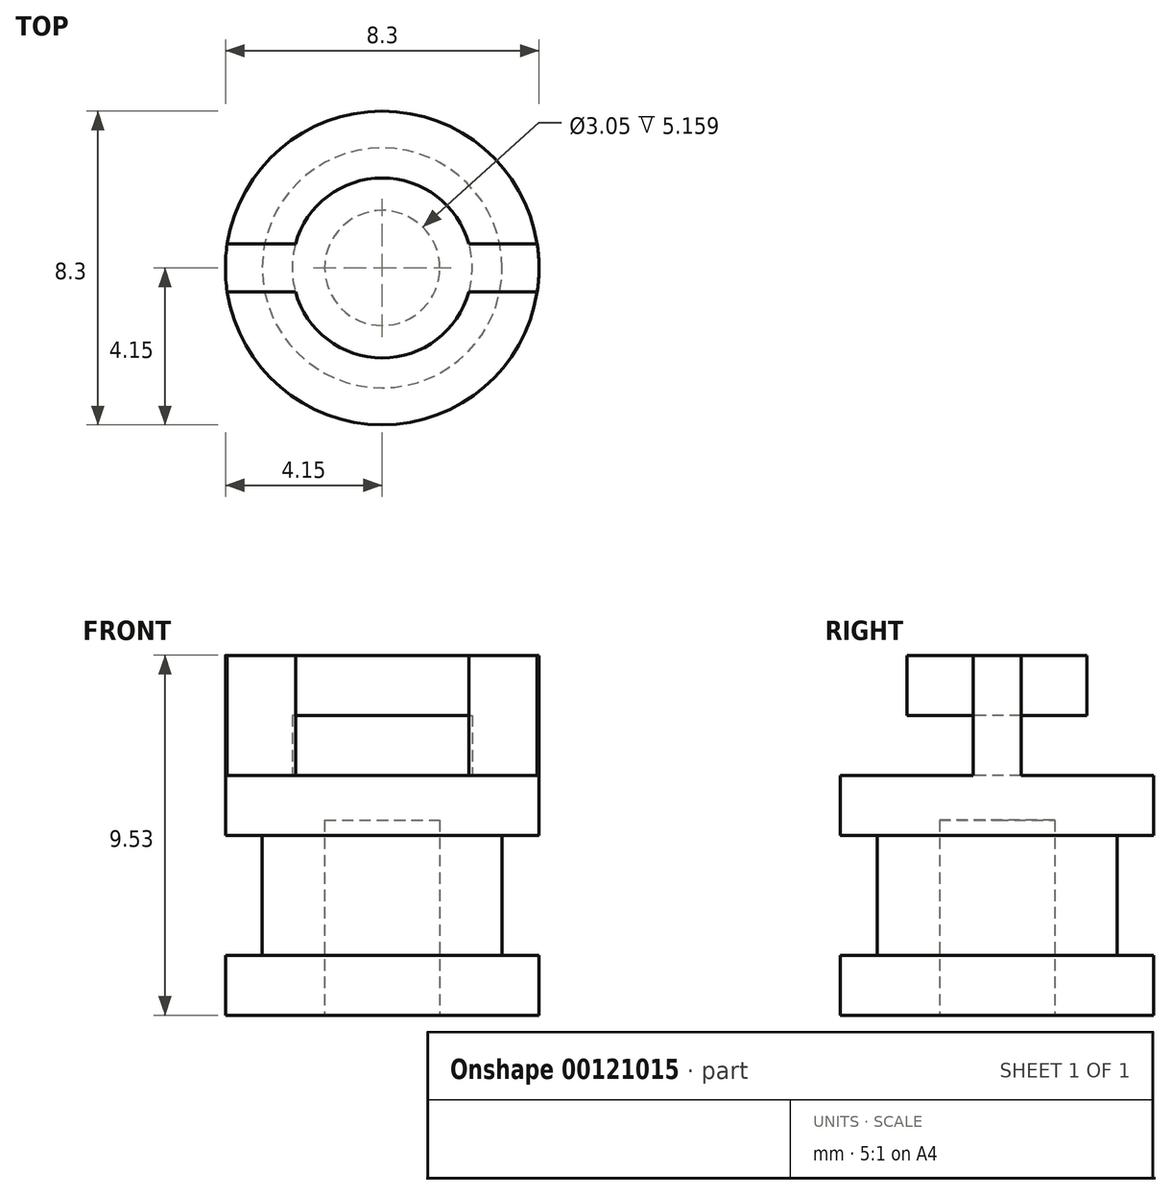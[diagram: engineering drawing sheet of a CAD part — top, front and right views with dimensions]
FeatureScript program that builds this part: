
annotation { "Feature Type Name" : "Feature", "Feature Type Description" : "" }
export const myFeature = defineFeature(function(context is Context, id is Id, definition is map)
    precondition{}
    {
        {
            var Q0;
            Q0=qCreatedBy(makeId("Top.planeOp"),FACE);
            var sketch = newSketch(context, id + "F0", { "sketchPlane" : qUnion([Q0])});
            skCircle(sketch, "E0", {"center": v(0, 0) * mm, "radius": 4.15 * mm});
            skSolve(sketch);
        }
        {
            var Q0;
            Q0=qSketchRegion(id+"F0",true);
            extrude(context, id + "F1", {"entities" : qUnion([Q0]), "depth" : 1.59 * mm});
        }
        {
            var Q0;
            Q0=qCreatedBy(makeId("Top.planeOp"),FACE);
            cPlane(context, id + "F2", {"entities" : qUnion([Q0]), "cplaneType" : CPlaneType.OFFSET, "offset" : 6.35 * mm, "width" : 152.4 * mm, "height" : 152.4 * mm});
        }
        {
            var Q0;
            Q0=qCreatedBy(id+"F2.planeOp",FACE);
            var sketch = newSketch(context, id + "F3", { "sketchPlane" : qUnion([Q0])});
            skCircle(sketch, "E1.0", {"center": v(0, 0) * mm, "radius": 4.15 * mm});
            skSolve(sketch);
        }
        {
            var Q0;
            Q0=qSketchRegion(id+"F3",true);
            extrude(context, id + "F4", {"entities" : qUnion([Q0]), "oppositeDirection" : true, "depth" : 1.59 * mm});
        }
        {
            var Q0;
            Q0=makeQuery(id+"F4.opExtrude","CAP_FACE",FACE,{"disambiguationData":[OSD([sQuery(id+"F3.wireOp",EDGE,"E1.0")])],"isStart":true});
            cPlane(context, id + "F5", {"entities" : qUnion([Q0]), "cplaneType" : CPlaneType.OFFSET, "offset" : 1.59 * mm, "width" : 152.4 * mm, "height" : 152.4 * mm});
        }
        {
            var Q0;
            Q0=qCreatedBy(id+"F5.planeOp",FACE);
            var sketch = newSketch(context, id + "F6", { "sketchPlane" : qUnion([Q0])});
            skCircle(sketch, "E2", {"center": v(0, 0) * mm, "radius": 2.38 * mm});
            skSolve(sketch);
        }
        {
            var Q0;
            Q0=qSketchRegion(id+"F6",true);
            extrude(context, id + "F7", {"entities" : qUnion([Q0]), "depth" : 1.59 * mm});
        }
        {
            var Q0;
            Q0=makeQuery(id+"F4.opExtrude","CAP_FACE",FACE,{"disambiguationData":[OSD([sQuery(id+"F3.wireOp",EDGE,"E1.0")])],"isStart":true});
            var sketch = newSketch(context, id + "F8", { "sketchPlane" : qUnion([Q0])});
            skLineSegment(sketch, "E3", {"start": v(-4.15, 0) * mm, "end": v(4.15, 0) * mm, "construction": true});
            skLineSegment(sketch, "E4", {"start": v(-4.1, -0.63) * mm, "end": v(4.1, -0.63) * mm});
            skLineSegment(sketch, "E5", {"start": v(-4.1, 0.64) * mm, "end": v(4.1, 0.64) * mm});
            skLineSegment(sketch, "E6", {"start": v(0, -0.63) * mm, "end": v(0, 0.63) * mm, "construction": true});
            skPoint(sketch, "E7", {"position": v(0, 0) * mm});
            skArc(sketch, "E8.0", {"start": v(-4.1, 0.63) * mm, "mid": v(-4.15, 0) * mm, "end": v(-4.1, -0.63) * mm});
            skArc(sketch, "E9.trimOffspring", {"start": v(4.1, -0.64) * mm, "mid": v(4.15, 0) * mm, "end": v(4.1, 0.64) * mm});
            skArc(sketch, "E10.0", {"start": v(-2.3, 0.63) * mm, "mid": v(-2.38, 0) * mm, "end": v(-2.3, -0.63) * mm});
            skArc(sketch, "E11.trimOffspring", {"start": v(2.3, -0.63) * mm, "mid": v(2.38, 0) * mm, "end": v(2.3, 0.64) * mm});
            skSolve(sketch);
        }
        {
            var Q0;
            {var subQ0=sQuery(id+"F8.wireOp",EDGE,"E9.trimOffspring");Q0=makeQuery(id+"F8.imprint","IMPRINT",FACE,{"disambiguationData":[TD([[makeQuery(id+"F8.imprint","IMPRINT",EDGE,{"derivedFrom":subQ0}),1.0]])]});}
            var Q1;
            {var subQ0=sQuery(id+"F8.wireOp",EDGE,"E8.0");Q1=makeQuery(id+"F8.imprint","IMPRINT",FACE,{"disambiguationData":[TD([[makeQuery(id+"F8.imprint","IMPRINT",EDGE,{"derivedFrom":subQ0}),1.0]])]});}
            var Q2;
            Q2=makeQuery(id+"F7.opExtrude","CAP_FACE",FACE,{"disambiguationData":[OSD([sQuery(id+"F6.wireOp",EDGE,"E2")])],"isStart":false});
            extrude(context, id + "F9", {"entities" : qUnion([Q0, Q1]), "operationType" : NewBodyOperationType.ADD, "endBound" : BoundingType.UP_TO_SURFACE, "endBoundEntityFace" : qUnion([Q2]), "depth" : 25.4 * mm});
        }
        {
            var Q0;
            Q0=makeQuery(id+"F1.opExtrude","CAP_FACE",FACE,{"disambiguationData":[OSD([sQuery(id+"F0.wireOp",EDGE,"E0")])],"isStart":false});
            var sketch = newSketch(context, id + "F10", { "sketchPlane" : qUnion([Q0])});
            skCircle(sketch, "E12", {"center": v(0, 0) * mm, "radius": 3.17 * mm});
            skSolve(sketch);
        }
        {
            var Q0;
            Q0=qSketchRegion(id+"F10",true);
            var Q1;
            Q1=makeQuery(id+"F4.opExtrude","CAP_FACE",FACE,{"disambiguationData":[OSD([sQuery(id+"F3.wireOp",EDGE,"E1.0")])],"isStart":false});
            extrude(context, id + "F11", {"entities" : qUnion([Q0]), "operationType" : NewBodyOperationType.ADD, "endBound" : BoundingType.UP_TO_NEXT, "endBoundEntityFace" : qUnion([Q1]), "depth" : 25.4 * mm});
        }
        {
            var Q0;
            Q0=makeQuery(id+"F1.opExtrude","CAP_FACE",FACE,{"disambiguationData":[OSD([sQuery(id+"F0.wireOp",EDGE,"E0")])],"isStart":true});
            var sketch = newSketch(context, id + "F12", { "sketchPlane" : qUnion([Q0])});
            skCircle(sketch, "E13", {"center": v(0, 0) * mm, "radius": 1.52 * mm});
            skSolve(sketch);
        }
        {
            var Q0;
            Q0=qSketchRegion(id+"F12",true);
            extrude(context, id + "F13", {"entities" : qUnion([Q0]), "operationType" : NewBodyOperationType.REMOVE, "oppositeDirection" : true, "depth" : 5.16 * mm});
        }
        {
            var Q0;
            Q0=makeQuery(id+"F1.opExtrude","CAP_FACE",FACE,{"disambiguationData":[OSD([sQuery(id+"F0.wireOp",EDGE,"E0")])],"isStart":true});
            var sketch = newSketch(context, id + "F14", { "sketchPlane" : qUnion([Q0])});
            skLineSegment(sketch, "E14", {"start": v(-2.93, -2.93) * mm, "end": v(2.93, 2.93) * mm});
            skSolve(sketch);
        }
    });
